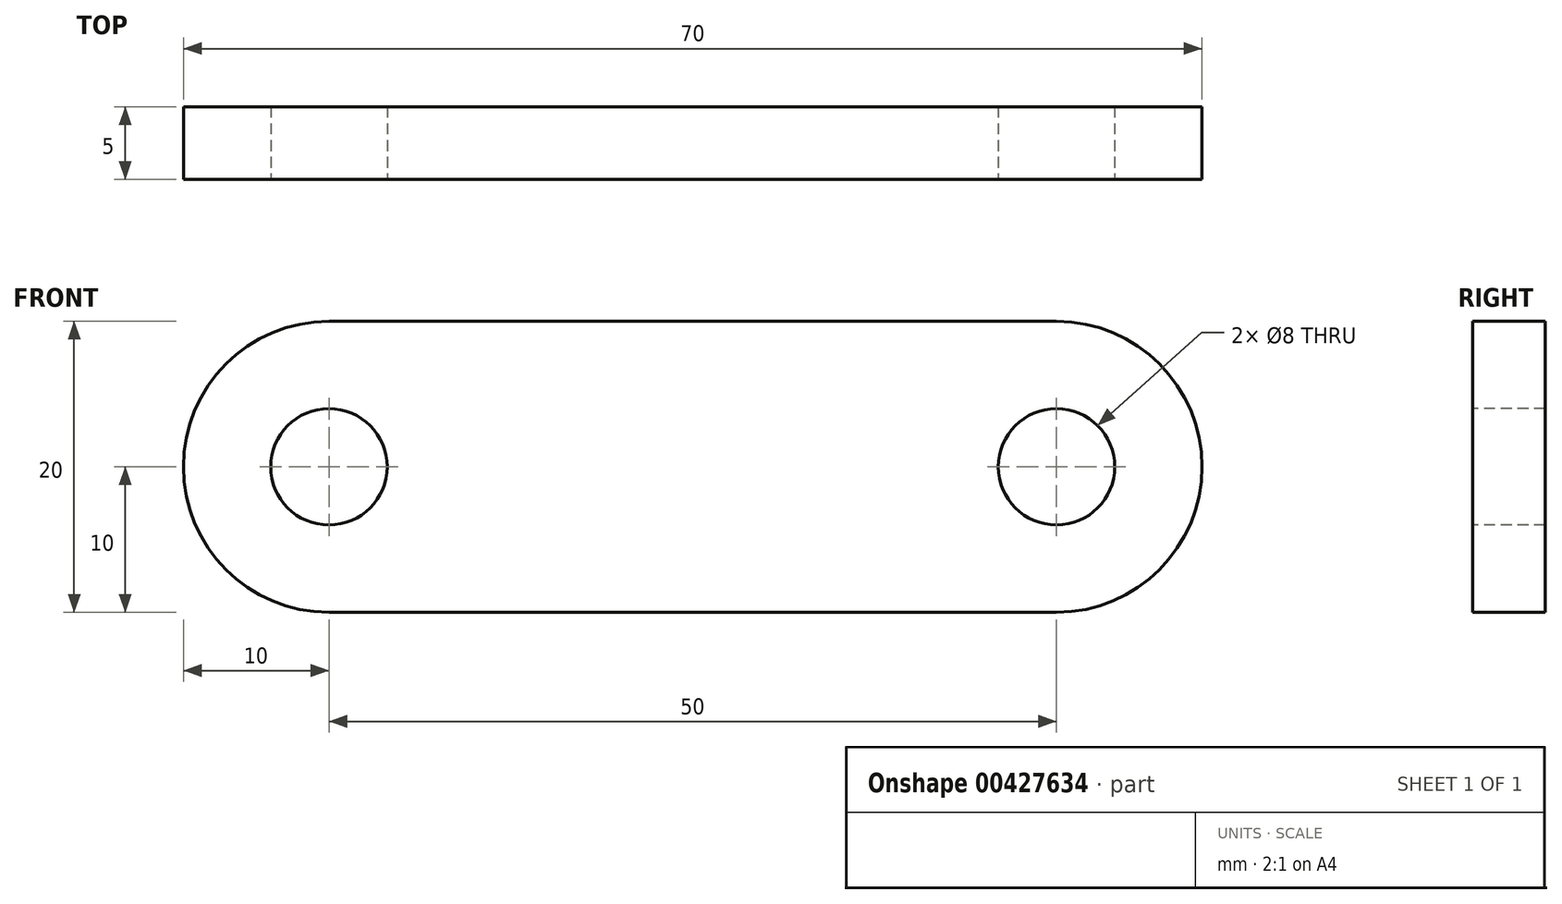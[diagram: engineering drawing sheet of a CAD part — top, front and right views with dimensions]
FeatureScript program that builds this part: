
annotation { "Feature Type Name" : "Feature", "Feature Type Description" : "" }
export const myFeature = defineFeature(function(context is Context, id is Id, definition is map)
    precondition{}
    {
        {
            var Q0;
            Q0=qCreatedBy(makeId("Front.planeOp"),FACE);
            var sketch = newSketch(context, id + "F0", { "sketchPlane" : qUnion([Q0])});
            skLineSegment(sketch, "E0.bottom", {"start": v(0, 0) * mm, "end": v(70, 0) * mm});
            skLineSegment(sketch, "E0.top", {"start": v(0, 20) * mm, "end": v(70, 20) * mm});
            skLineSegment(sketch, "E0.left", {"start": v(0, 0) * mm, "end": v(0, 20) * mm});
            skLineSegment(sketch, "E0.right", {"start": v(70, 0) * mm, "end": v(70, 20) * mm});
            skSolve(sketch);
        }
        {
            var Q0;
            Q0=qSketchRegion(id+"F0",true);
            extrude(context, id + "F1", {"entities" : qUnion([Q0]), "depth" : 5 * mm});
        }
        {
            var Q0;
            Q0=makeQuery(id+"F1.opExtrude","SWEPT_EDGE",EDGE,{"disambiguationData":[OSD([sQuery(id+"F0.wireOp",EDGE,"E0.top"),sQuery(id+"F0.wireOp",EDGE,"E0.right")])]});
            var Q1;
            Q1=makeQuery(id+"F1.opExtrude","SWEPT_EDGE",EDGE,{"disambiguationData":[OSD([sQuery(id+"F0.wireOp",EDGE,"E0.bottom"),sQuery(id+"F0.wireOp",EDGE,"E0.right")])]});
            var Q2;
            Q2=makeQuery(id+"F1.opExtrude","SWEPT_EDGE",EDGE,{"disambiguationData":[OSD([sQuery(id+"F0.wireOp",EDGE,"E0.top"),sQuery(id+"F0.wireOp",EDGE,"E0.left")])]});
            var Q3;
            Q3=makeQuery(id+"F1.opExtrude","SWEPT_EDGE",EDGE,{"disambiguationData":[OSD([sQuery(id+"F0.wireOp",EDGE,"E0.bottom"),sQuery(id+"F0.wireOp",EDGE,"E0.left")])]});
            fillet(context, id + "F2", {"entities" : qUnion([Q0, Q1, Q2, Q3]), "radius" : 10 * mm, "tangentPropagation" : true, "allowEdgeOverflow" : false});
        }
        {
            var Q0;
            Q0=makeQuery(id+"F1.opExtrude","CAP_FACE",FACE,{"disambiguationData":[OSD([sQuery(id+"F0.wireOp",EDGE,"E0.bottom"),sQuery(id+"F0.wireOp",EDGE,"E0.top"),sQuery(id+"F0.wireOp",EDGE,"E0.left"),sQuery(id+"F0.wireOp",EDGE,"E0.right")])],"isStart":false});
            var sketch = newSketch(context, id + "F3", { "sketchPlane" : qUnion([Q0])});
            skCircle(sketch, "E1", {"center": v(10, 10) * mm, "radius": 4 * mm});
            skCircle(sketch, "E2", {"center": v(60, 10) * mm, "radius": 4 * mm});
            skSolve(sketch);
        }
        {
            var Q0;
            Q0=qSketchRegion(id+"F3",true);
            extrude(context, id + "F4", {"entities" : qUnion([Q0]), "operationType" : NewBodyOperationType.REMOVE, "endBound" : BoundingType.THROUGH_ALL, "oppositeDirection" : true, "depth" : 25 * mm});
        }
    });
